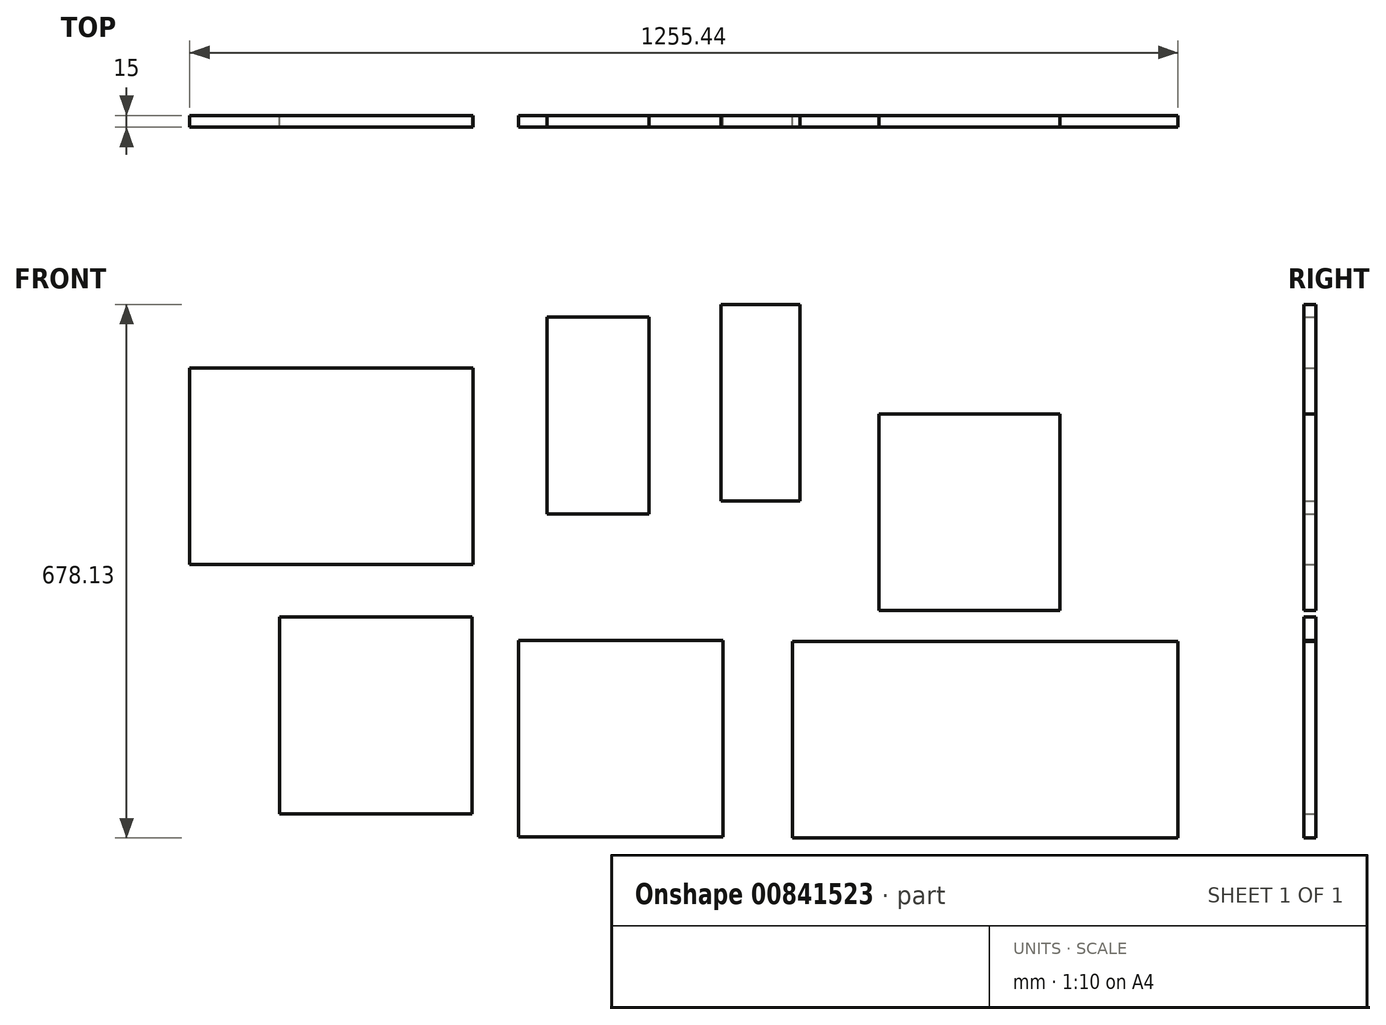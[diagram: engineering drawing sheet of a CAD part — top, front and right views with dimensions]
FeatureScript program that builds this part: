
annotation { "Feature Type Name" : "Feature", "Feature Type Description" : "" }
export const myFeature = defineFeature(function(context is Context, id is Id, definition is map)
    precondition{}
    {
        {
            var Q0;
            Q0=qCreatedBy(makeId("Front.planeOp"),FACE);
            var sketch = newSketch(context, id + "F0", { "sketchPlane" : qUnion([Q0])});
            skLineSegment(sketch, "E0.bottom", {"start": v(-170.9, 261.95) * mm, "end": v(-40.9, 261.95) * mm});
            skLineSegment(sketch, "E0.top", {"start": v(-170.9, 11.95) * mm, "end": v(-40.9, 11.95) * mm});
            skLineSegment(sketch, "E0.left", {"start": v(-170.9, 261.95) * mm, "end": v(-170.9, 11.95) * mm});
            skLineSegment(sketch, "E0.right", {"start": v(-40.9, 261.95) * mm, "end": v(-40.9, 11.95) * mm});
            skLineSegment(sketch, "E1.bottom", {"start": v(50.6, 278.36) * mm, "end": v(150.6, 278.36) * mm});
            skLineSegment(sketch, "E1.top", {"start": v(50.6, 28.36) * mm, "end": v(150.6, 28.36) * mm});
            skLineSegment(sketch, "E1.left", {"start": v(50.6, 278.36) * mm, "end": v(50.6, 28.36) * mm});
            skLineSegment(sketch, "E1.right", {"start": v(150.6, 278.36) * mm, "end": v(150.6, 28.36) * mm});
            skLineSegment(sketch, "E2.bottom", {"start": v(250.89, 139.27) * mm, "end": v(480.89, 139.27) * mm});
            skLineSegment(sketch, "E2.top", {"start": v(250.89, -110.73) * mm, "end": v(480.89, -110.73) * mm});
            skLineSegment(sketch, "E2.left", {"start": v(250.89, 139.27) * mm, "end": v(250.89, -110.73) * mm});
            skLineSegment(sketch, "E2.right", {"start": v(480.89, 139.27) * mm, "end": v(480.89, -110.73) * mm});
            skLineSegment(sketch, "E3.bottom", {"start": v(-624.61, 197.74) * mm, "end": v(-264.61, 197.74) * mm});
            skLineSegment(sketch, "E3.top", {"start": v(-624.61, -52.26) * mm, "end": v(-264.61, -52.26) * mm});
            skLineSegment(sketch, "E3.left", {"start": v(-624.61, 197.74) * mm, "end": v(-624.61, -52.26) * mm});
            skLineSegment(sketch, "E3.right", {"start": v(-264.61, 197.74) * mm, "end": v(-264.61, -52.26) * mm});
            skLineSegment(sketch, "E4.bottom", {"start": v(-510.63, -118.8) * mm, "end": v(-265.63, -118.8) * mm});
            skLineSegment(sketch, "E4.top", {"start": v(-510.63, -368.8) * mm, "end": v(-265.63, -368.8) * mm});
            skLineSegment(sketch, "E4.left", {"start": v(-510.63, -118.8) * mm, "end": v(-510.63, -368.8) * mm});
            skLineSegment(sketch, "E4.right", {"start": v(-265.63, -118.8) * mm, "end": v(-265.63, -368.8) * mm});
            skLineSegment(sketch, "E5.bottom", {"start": v(-207.07, -148.5) * mm, "end": v(52.93, -148.5) * mm});
            skLineSegment(sketch, "E5.top", {"start": v(-207.07, -398.5) * mm, "end": v(52.93, -398.5) * mm});
            skLineSegment(sketch, "E5.left", {"start": v(-207.07, -148.5) * mm, "end": v(-207.07, -398.5) * mm});
            skLineSegment(sketch, "E5.right", {"start": v(52.93, -148.5) * mm, "end": v(52.93, -398.5) * mm});
            skLineSegment(sketch, "E6.bottom", {"start": v(140.83, -149.77) * mm, "end": v(630.83, -149.77) * mm});
            skLineSegment(sketch, "E6.top", {"start": v(140.83, -399.77) * mm, "end": v(630.83, -399.77) * mm});
            skLineSegment(sketch, "E6.left", {"start": v(140.83, -149.77) * mm, "end": v(140.83, -399.77) * mm});
            skLineSegment(sketch, "E6.right", {"start": v(630.83, -149.77) * mm, "end": v(630.83, -399.77) * mm});
            skSolve(sketch);
        }
        {
            var Q0;
            Q0=makeQuery(id+"F0.imprint","IMPRINT",FACE,{"disambiguationData":[TD([[makeQuery(id+"F0.imprint","IMPRINT",EDGE,{"derivedFrom":sQuery(id+"F0.wireOp",EDGE,"E3.bottom")}),-1.0]])]});
            extrude(context, id + "F1", {"entities" : qUnion([Q0]), "depth" : 15 * mm, "offsetDistance" : 25 * mm});
        }
        {
            var Q0;
            Q0=makeQuery(id+"F0.imprint","IMPRINT",FACE,{"disambiguationData":[TD([[makeQuery(id+"F0.imprint","IMPRINT",EDGE,{"derivedFrom":sQuery(id+"F0.wireOp",EDGE,"E0.bottom")}),-1.0]])]});
            extrude(context, id + "F2", {"entities" : qUnion([Q0]), "depth" : 15 * mm, "offsetDistance" : 25 * mm});
        }
        {
            var Q0;
            Q0=makeQuery(id+"F0.imprint","IMPRINT",FACE,{"disambiguationData":[TD([[makeQuery(id+"F0.imprint","IMPRINT",EDGE,{"derivedFrom":sQuery(id+"F0.wireOp",EDGE,"E1.bottom")}),-1.0]])]});
            extrude(context, id + "F3", {"entities" : qUnion([Q0]), "depth" : 15 * mm, "offsetDistance" : 25 * mm});
        }
        {
            var Q0;
            Q0=makeQuery(id+"F0.imprint","IMPRINT",FACE,{"disambiguationData":[TD([[makeQuery(id+"F0.imprint","IMPRINT",EDGE,{"derivedFrom":sQuery(id+"F0.wireOp",EDGE,"E2.bottom")}),-1.0]])]});
            extrude(context, id + "F4", {"entities" : qUnion([Q0]), "depth" : 15 * mm, "offsetDistance" : 25 * mm});
        }
        {
            var Q0;
            Q0=makeQuery(id+"F0.imprint","IMPRINT",FACE,{"disambiguationData":[TD([[makeQuery(id+"F0.imprint","IMPRINT",EDGE,{"derivedFrom":sQuery(id+"F0.wireOp",EDGE,"E4.bottom")}),-1.0]])]});
            extrude(context, id + "F5", {"entities" : qUnion([Q0]), "depth" : 15 * mm, "offsetDistance" : 25 * mm});
        }
        {
            var Q0;
            Q0=makeQuery(id+"F0.imprint","IMPRINT",FACE,{"disambiguationData":[TD([[makeQuery(id+"F0.imprint","IMPRINT",EDGE,{"derivedFrom":sQuery(id+"F0.wireOp",EDGE,"E5.bottom")}),-1.0]])]});
            extrude(context, id + "F6", {"entities" : qUnion([Q0]), "depth" : 15 * mm, "offsetDistance" : 25 * mm});
        }
        {
            var Q0;
            Q0=makeQuery(id+"F0.imprint","IMPRINT",FACE,{"disambiguationData":[TD([[makeQuery(id+"F0.imprint","IMPRINT",EDGE,{"derivedFrom":sQuery(id+"F0.wireOp",EDGE,"E6.bottom")}),-1.0]])]});
            extrude(context, id + "F7", {"entities" : qUnion([Q0]), "depth" : 15 * mm, "offsetDistance" : 25 * mm});
        }
    });
